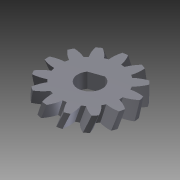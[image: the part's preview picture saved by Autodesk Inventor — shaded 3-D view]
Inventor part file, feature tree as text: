
AUTODESK INVENTOR PART (.ipt)
format: ipt  version: 2012 (Build 160160000, 160)  size: 306,688 bytes
history: native  units: mm (DEFAULTED — no unit token found)
features: plane x3, other x3, sketch x3, extrude x2, reference x2
ambient origin geometry x8: Origin, YZ Plane, XZ Plane, XY Plane, X Axis, Y Axis, Z Axis, Center Point
bodies: Solid1 (feature_tree)
feature tree (13):
  extrude  "Extrusion1"  Depth=4.0mm TaperAngle=0.0deg
  plane  "Work Plane2"
  plane  "Work Plane8"
  plane  "Work Plane9"
  other  "Spur Gear"
  extrude  "Extrusion2"  Depth=10.0mm TaperAngle=0.0deg
  sketch  "Sketch1"  dims[d0=22.612246mm d1=4.0mm d2=0.0mm]
  sketch  "Sketch2"  dims[d3=19.673383mm d4=10.0mm d5=0.0mm]
  other  "Srf1"
  sketch  "Sketch3"  dims[d16=17.403377mm d17=0.0mm d34=2.41661mm d39=0.0mm d41=0.0mm d43=17.403377mm d46=17.403377mm d47=0.0mm d48=0.0mm d49=10.0mm d50=0.0mm]
  reference  "Reference1"
  reference  "Reference2"
  other  "Pitch Diameter"
